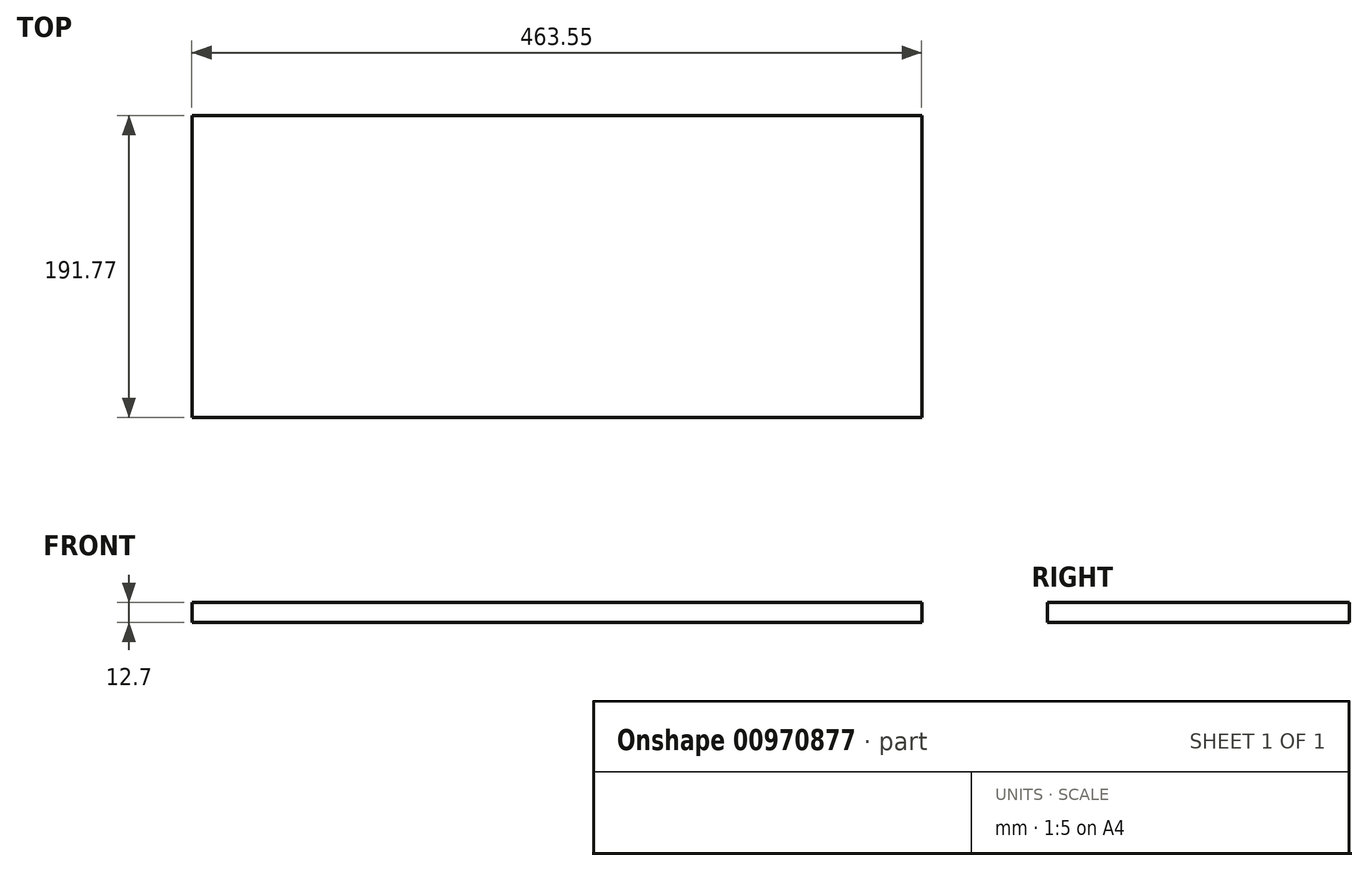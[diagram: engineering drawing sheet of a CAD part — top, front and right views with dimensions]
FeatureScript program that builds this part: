
annotation { "Feature Type Name" : "Feature", "Feature Type Description" : "" }
export const myFeature = defineFeature(function(context is Context, id is Id, definition is map)
    precondition{}
    {
        {
            var Q0;
            Q0=qCreatedBy(makeId("Top.planeOp"),FACE);
            var sketch = newSketch(context, id + "F0", { "sketchPlane" : qUnion([Q0])});
            skLineSegment(sketch, "E0.bottom", {"start": v(-171.56, 75.23) * mm, "end": v(292, 75.23) * mm});
            skLineSegment(sketch, "E0.top", {"start": v(-171.56, -116.54) * mm, "end": v(292, -116.54) * mm});
            skLineSegment(sketch, "E0.left", {"start": v(-171.56, 75.23) * mm, "end": v(-171.56, -116.54) * mm});
            skLineSegment(sketch, "E0.right", {"start": v(292, 75.23) * mm, "end": v(292, -116.54) * mm});
            skSolve(sketch);
        }
        {
            var Q0;
            Q0=qSketchRegion(id+"F0",true);
            extrude(context, id + "F1", {"entities" : qUnion([Q0]), "depth" : 12.7 * mm, "offsetDistance" : 25.4 * mm});
        }
    });
